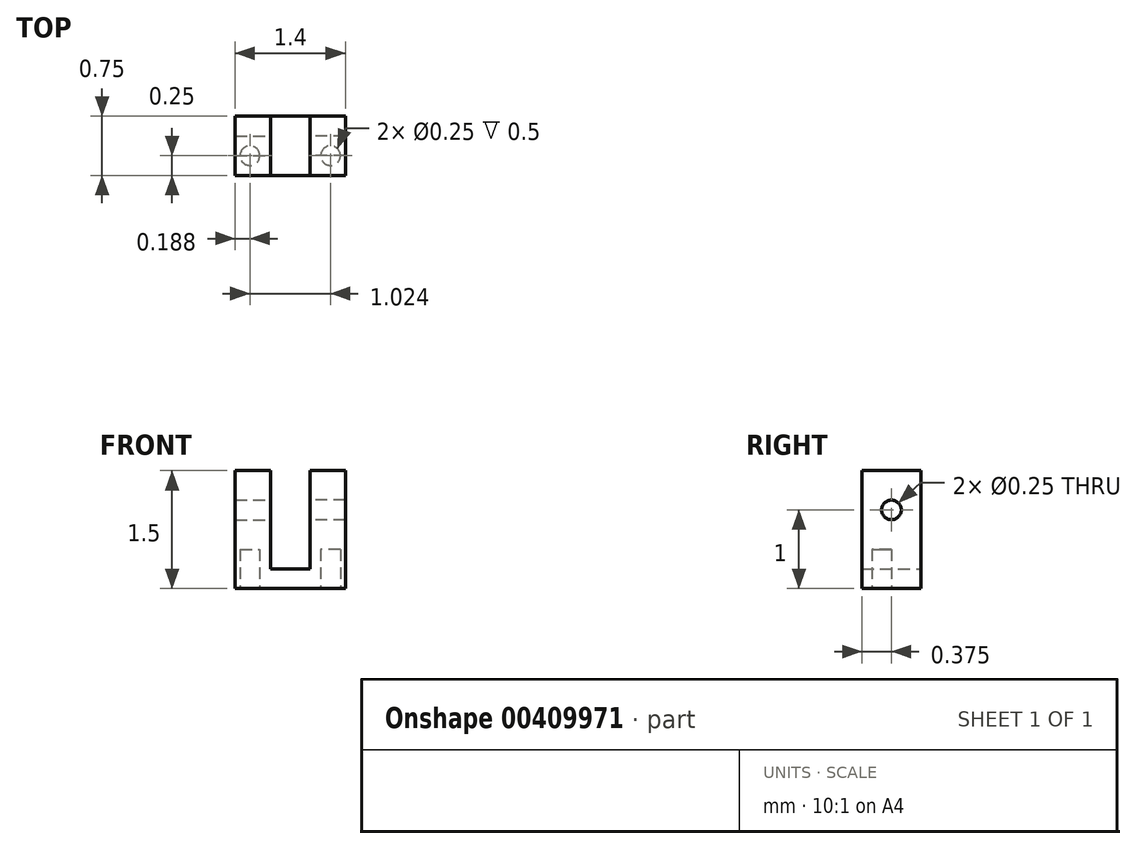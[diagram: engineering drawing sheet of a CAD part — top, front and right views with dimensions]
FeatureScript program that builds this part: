
annotation { "Feature Type Name" : "Feature", "Feature Type Description" : "" }
export const myFeature = defineFeature(function(context is Context, id is Id, definition is map)
    precondition{}
    {
        {
            var Q0;
            Q0=qCreatedBy(makeId("Front.planeOp"),FACE);
            var sketch = newSketch(context, id + "F0", { "sketchPlane" : qUnion([Q0])});
            skLineSegment(sketch, "E0.bottom", {"start": v(-0.7, 1.25) * mm, "end": v(-0.25, 1.25) * mm});
            skLineSegment(sketch, "E0.left", {"start": v(-0.7, 1.25) * mm, "end": v(-0.7, -0.25) * mm});
            skLineSegment(sketch, "E0.right", {"start": v(-0.25, 1.25) * mm, "end": v(-0.25, 0) * mm});
            skLineSegment(sketch, "E1.bottom", {"start": v(-0.25, 0) * mm, "end": v(0, 0) * mm});
            skLineSegment(sketch, "E1.top", {"start": v(-0.7, -0.25) * mm, "end": v(0, -0.25) * mm});
            skLineSegment(sketch, "E1.right", {"start": v(0, 0) * mm, "end": v(0, -0.25) * mm});
            skSolve(sketch);
        }
        {
            var Q0;
            Q0=makeQuery(id+"F0.imprint","IMPRINT",FACE,{"disambiguationData":[TD([[makeQuery(id+"F0.imprint","IMPRINT",EDGE,{"derivedFrom":sQuery(id+"F0.wireOp",EDGE,"E0.bottom")}),-1.0]])]});
            extrude(context, id + "F1", {"entities" : qUnion([Q0]), "depth" : 0.75 * mm});
        }
        {
            var Q0;
            Q0=makeQuery(id+"F1.opExtrude","SWEPT_FACE",FACE,{"disambiguationData":[OSD([sQuery(id+"F0.wireOp",EDGE,"E0.right")])]});
            var sketch = newSketch(context, id + "F2", { "sketchPlane" : qUnion([Q0])});
            skCircle(sketch, "E2", {"center": v(-0.38, 0.75) * mm, "radius": 0.12 * mm});
            skSolve(sketch);
        }
        {
            var Q0;
            Q0=makeQuery(id+"F2.imprint","IMPRINT",FACE,{"disambiguationData":[TD([[makeQuery(id+"F2.imprint","IMPRINT",EDGE,{"derivedFrom":sQuery(id+"F2.wireOp",EDGE,"E2")}),1.0]])]});
            extrude(context, id + "F3", {"entities" : qUnion([Q0]), "operationType" : NewBodyOperationType.REMOVE, "oppositeDirection" : true, "depth" : 25 * mm});
        }
        {
            var Q0;
            Q0=makeQuery(id+"F1.opExtrude","SWEPT_FACE",FACE,{"disambiguationData":[OSD([sQuery(id+"F0.wireOp",EDGE,"E1.top")])]});
            var sketch = newSketch(context, id + "F4", { "sketchPlane" : qUnion([Q0])});
            skCircle(sketch, "E3", {"center": v(-0.51, 0.5) * mm, "radius": 0.12 * mm});
            skSolve(sketch);
        }
        {
            var Q0;
            Q0=makeQuery(id+"F4.imprint","IMPRINT",FACE,{"disambiguationData":[TD([[makeQuery(id+"F4.imprint","IMPRINT",EDGE,{"derivedFrom":sQuery(id+"F4.wireOp",EDGE,"E3")}),1.0]])]});
            extrude(context, id + "F5", {"entities" : qUnion([Q0]), "operationType" : NewBodyOperationType.REMOVE, "oppositeDirection" : true, "depth" : 0.5 * mm});
        }
        {
            var Q0;
            Q0=makeQuery(id+"F1.opExtrude","SWEPT_BODY",BODY,{"disambiguationData":[OSD([sQuery(id+"F0.wireOp",EDGE,"E0.bottom"),sQuery(id+"F0.wireOp",EDGE,"E0.left"),sQuery(id+"F0.wireOp",EDGE,"E0.right"),sQuery(id+"F0.wireOp",EDGE,"E1.bottom"),sQuery(id+"F0.wireOp",EDGE,"E1.top"),sQuery(id+"F0.wireOp",EDGE,"E1.right")])]});
            var Q1;
            Q1=makeQuery(id+"F1.opExtrude","SWEPT_FACE",FACE,{"disambiguationData":[OSD([sQuery(id+"F0.wireOp",EDGE,"E1.right")])]});
            mirror(context, id + "F6", {"operationType" : NewBodyOperationType.ADD, "entities" : qUnion([Q0]), "mirrorPlane" : qUnion([Q1])});
        }
    });
